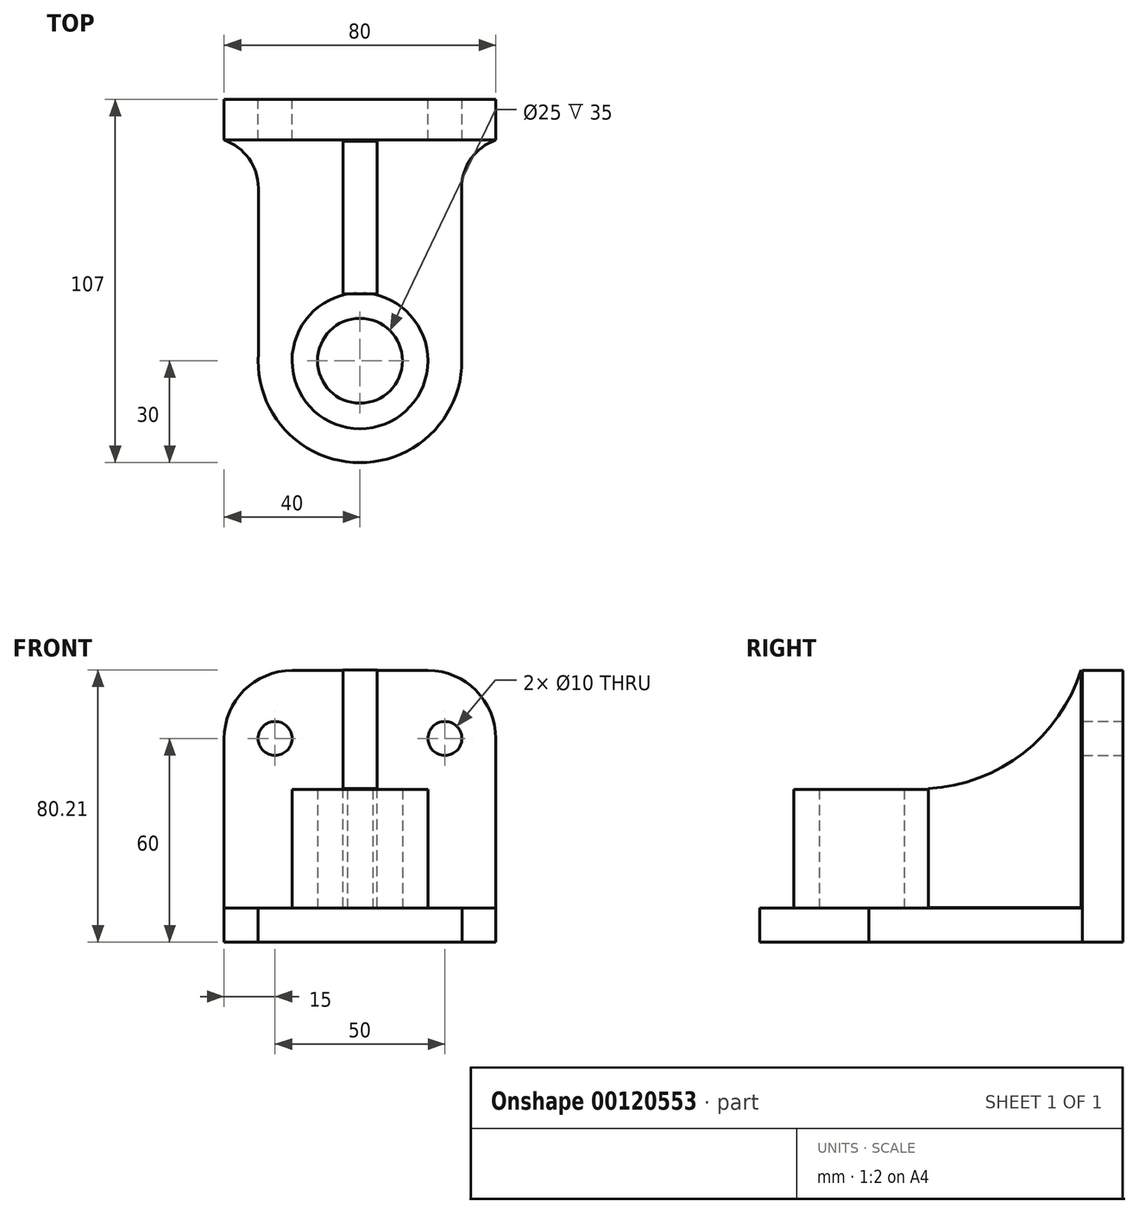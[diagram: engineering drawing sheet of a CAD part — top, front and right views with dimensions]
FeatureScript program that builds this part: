
annotation { "Feature Type Name" : "Feature", "Feature Type Description" : "" }
export const myFeature = defineFeature(function(context is Context, id is Id, definition is map)
    precondition{}
    {
        {
            var Q0;
            Q0=qCreatedBy(makeId("Front.planeOp"),FACE);
            var sketch = newSketch(context, id + "F0", { "sketchPlane" : qUnion([Q0])});
            skLineSegment(sketch, "E0.bottom", {"start": v(-40, 40) * mm, "end": v(40, 40) * mm});
            skLineSegment(sketch, "E0.top", {"start": v(-40, -40) * mm, "end": v(40, -40) * mm});
            skLineSegment(sketch, "E0.left", {"start": v(-40, 40) * mm, "end": v(-40, -40) * mm});
            skLineSegment(sketch, "E0.right", {"start": v(40, 40) * mm, "end": v(40, -40) * mm});
            skCircle(sketch, "E1", {"center": v(-25, 20) * mm, "radius": 5 * mm});
            skCircle(sketch, "E2.MirrorC", {"center": v(25, 20) * mm, "radius": 5 * mm});
            skSolve(sketch);
        }
        {
            var Q0;
            Q0 = qSketchRegion(id + "F0", true);
            var Q1;
            Q1=makeQuery(id+"F0.imprint","IMPRINT",FACE,{"disambiguationData":[TD([[makeQuery(id+"F0.imprint","IMPRINT",EDGE,{"derivedFrom":sQuery(id+"F0.wireOp",EDGE,"E0.bottom")}),-1.0]])]});
            extrude(context, id + "F1", {"entities" : qUnion([Q0, Q1]), "depth" : 12 * mm});
        }
        {
            var Q0;
            Q0=makeQuery(id+"F1.opExtrude","SWEPT_EDGE",EDGE,{"disambiguationData":[OSD([sQuery(id+"F0.wireOp",EDGE,"E0.bottom"),sQuery(id+"F0.wireOp",EDGE,"E0.right")])]});
            var Q1;
            Q1=makeQuery(id+"F1.opExtrude","SWEPT_EDGE",EDGE,{"disambiguationData":[OSD([sQuery(id+"F0.wireOp",EDGE,"E0.bottom"),sQuery(id+"F0.wireOp",EDGE,"E0.left")])]});
            fillet(context, id + "F2", {"entities" : qUnion([Q0, Q1]), "radius" : 20 * mm, "tangentPropagation" : true, "allowEdgeOverflow" : false});
        }
        {
            var Q0;
            Q0=makeQuery(id+"F1.opExtrude","CAP_FACE",FACE,{"disambiguationData":[OSD([sQuery(id+"F0.wireOp",EDGE,"E0.bottom"),sQuery(id+"F0.wireOp",EDGE,"E0.top"),sQuery(id+"F0.wireOp",EDGE,"E0.left"),sQuery(id+"F0.wireOp",EDGE,"E0.right"),sQuery(id+"F0.wireOp",EDGE,"E1"),sQuery(id+"F0.wireOp",EDGE,"E2.MirrorC")])],"isStart":false});
            var sketch = newSketch(context, id + "F3", { "sketchPlane" : qUnion([Q0])});
            skLineSegment(sketch, "E3.bottom", {"start": v(-40, -40) * mm, "end": v(40, -40) * mm});
            skLineSegment(sketch, "E3.top", {"start": v(-40, -30) * mm, "end": v(40, -30) * mm});
            skLineSegment(sketch, "E3.left", {"start": v(-40, -40) * mm, "end": v(-40, -30) * mm});
            skLineSegment(sketch, "E3.right", {"start": v(40, -40) * mm, "end": v(40, -30) * mm});
            skSolve(sketch);
        }
        {
            var Q0;
            Q0 = qSketchRegion(id + "F3", true);
            var Q1;
            Q1=makeQuery(id+"F3.imprint","IMPRINT",FACE,{"disambiguationData":[TD([[makeQuery(id+"F3.imprint","IMPRINT",EDGE,{"derivedFrom":sQuery(id+"F3.wireOp",EDGE,"E3.bottom")}),1.0]])]});
            extrude(context, id + "F4", {"entities" : qUnion([Q0, Q1]), "operationType" : NewBodyOperationType.ADD, "depth" : 95 * mm});
        }
        {
            var Q0;
            Q0=makeQuery(id+"F4.opExtrude","SWEPT_FACE",FACE,{"disambiguationData":[OSD([sQuery(id+"F3.wireOp",EDGE,"E3.top")])]});
            var sketch = newSketch(context, id + "F5", { "sketchPlane" : qUnion([Q0])});
            skLineSegment(sketch, "E4", {"start": v(0, -107) * mm, "end": v(0, -77) * mm});
            skPoint(sketch, "E4.endSnap0", {"position": v(0, -107) * mm});
            skCircle(sketch, "E5", {"center": v(0, -77) * mm, "radius": 30 * mm});
            skLineSegment(sketch, "E6", {"start": v(-29.92, -74.86) * mm, "end": v(-29.92, -12) * mm});
            skLineSegment(sketch, "E7.MirrorCS", {"start": v(29.92, -74.86) * mm, "end": v(29.92, -12) * mm});
            skSolve(sketch);
        }
        {
            var Q0;
            {var subQ5=sQuery(id+"F5.wireOp",EDGE,"E6");Q0=makeQuery(id+"F5.imprint","IMPRINT",FACE,{"disambiguationData":[TD([[makeQuery(id+"F5.imprint","IMPRINT",EDGE,{"derivedFrom":subQ5}),1.0]])]});}
            var Q1;
            {var subQ5=sQuery(id+"F5.wireOp",EDGE,"E7.MirrorCS");Q1=makeQuery(id+"F5.imprint","IMPRINT",FACE,{"disambiguationData":[TD([[makeQuery(id+"F5.imprint","IMPRINT",EDGE,{"derivedFrom":subQ5}),-1.0]])]});}
            extrude(context, id + "F6", {"entities" : qUnion([Q0, Q1]), "operationType" : NewBodyOperationType.REMOVE, "oppositeDirection" : true, "depth" : 25 * mm});
        }
        {
            var Q0;
            Q0=makeQuery(id+"F6.boolean.opBoolean","COPY",EDGE,{"derivedFrom":makeQuery(id+"F6.opExtrude","SWEPT_EDGE",EDGE,{"disambiguationData":[OSD([sQuery(id+"F3.wireOp",EDGE,"E3.top"),sQuery(id+"F5.wireOp",EDGE,"E6")])]})});
            var Q1;
            Q1=makeQuery(id+"F6.boolean.opBoolean","COPY",EDGE,{"derivedFrom":makeQuery(id+"F6.opExtrude","SWEPT_EDGE",EDGE,{"disambiguationData":[OSD([sQuery(id+"F3.wireOp",EDGE,"E3.top"),sQuery(id+"F5.wireOp",EDGE,"E7.MirrorCS")])]})});
            fillet(context, id + "F7", {"entities" : qUnion([Q0, Q1]), "radius" : 15 * mm, "tangentPropagation" : true, "allowEdgeOverflow" : false});
        }
        {
            var Q0;
            Q0=makeQuery(id+"F4.opExtrude","SWEPT_FACE",FACE,{"disambiguationData":[OSD([sQuery(id+"F3.wireOp",EDGE,"E3.top")])]});
            var sketch = newSketch(context, id + "F8", { "sketchPlane" : qUnion([Q0])});
            skCircle(sketch, "E8", {"center": v(0, -77) * mm, "radius": 20 * mm});
            skCircle(sketch, "E9", {"center": v(0, -77) * mm, "radius": 12.5 * mm});
            skSolve(sketch);
        }
        {
            var Q0;
            Q0=makeQuery(id+"F8.imprint","IMPRINT",FACE,{"disambiguationData":[TD([[makeQuery(id+"F8.imprint","IMPRINT",EDGE,{"derivedFrom":sQuery(id+"F8.wireOp",EDGE,"E8")}),1.0]])]});
            extrude(context, id + "F9", {"entities" : qUnion([Q0]), "operationType" : NewBodyOperationType.ADD, "depth" : 35 * mm});
        }
        {
            var Q0;
            Q0=qCreatedBy(makeId("Right.planeOp"),FACE);
            var sketch = newSketch(context, id + "F10", { "sketchPlane" : qUnion([Q0])});
            skLineSegment(sketch, "E10", {"start": v(-12.36, -29.79) * mm, "end": v(-57.36, -29.79) * mm});
            skLineSegment(sketch, "E11", {"start": v(-57.36, -29.79) * mm, "end": v(-57.36, 5.21) * mm});
            skLineSegment(sketch, "E12", {"start": v(-12.36, -29.79) * mm, "end": v(-12.36, 40.21) * mm});
            skArc(sketch, "E13", {"start": v(-57.36, 5.21) * mm, "mid": v(-29.38, 15.67) * mm, "end": v(-12.36, 40.21) * mm});
            skSolve(sketch);
        }
        {
            var Q0;
            Q0 = qSketchRegion(id + "F10", true);
            var Q1;
            Q1=makeQuery(id+"F10.imprint","IMPRINT",FACE,{"disambiguationData":[TD([[makeQuery(id+"F10.imprint","IMPRINT",EDGE,{"derivedFrom":sQuery(id+"F10.wireOp",EDGE,"E10")}),-1.0]])]});
            extrude(context, id + "F11", {"entities" : qUnion([Q0, Q1]), "operationType" : NewBodyOperationType.ADD, "endBound" : BoundingType.SYMMETRIC, "depth" : 10 * mm});
        }
    });
